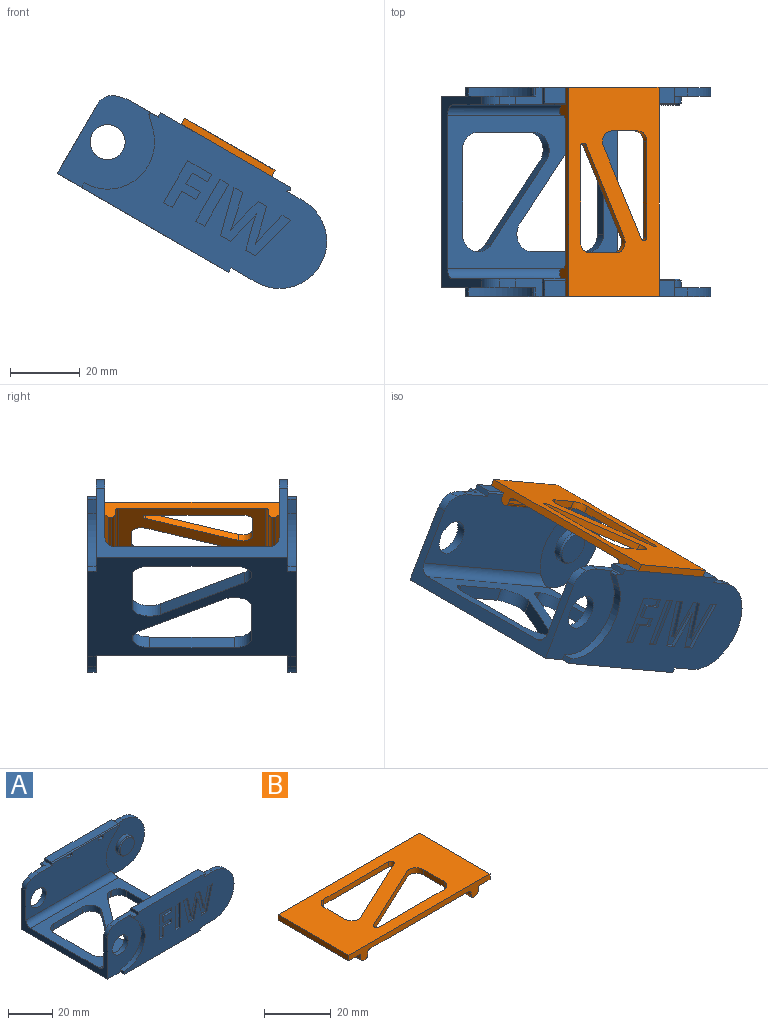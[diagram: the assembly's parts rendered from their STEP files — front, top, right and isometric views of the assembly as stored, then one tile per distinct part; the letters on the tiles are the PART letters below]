
ASSEMBLY  parts=2 mates=1
PART A: 175 faces, bbox 78.6x60x30 mm
  f0: plane 70.56x30mm, normal (0,1,0), area 1436.2mm2, adj f4,f7,f8,f9,f10,f11,f19,f20
  f1: plane 70.56x30mm, normal (0,-1,0), area 1436.2mm2, adj f4,f6,f13,f14,f15,f16,f25,f26
  f2: plane 60.26x23mm, normal (0,-1,0), area 1123.2mm2, adj f5,f20,f24,f28,f31,f42,f43,f63
  f3: plane 56.37x44mm, normal (0,0,1), area 1118.5mm2, adj f5,f46,f47,f48,f49,f50,f51,f52
  f4: plane 60x56.81mm, normal (0,0,-1), area 1989.1mm2, adj f0,f1,f5,f8,f13,f17,f19,f23
  f5: plane 55x22.95mm, normal (-1,0,0), area 293.6mm2, adj f2,f3,f4,f12,f17,f23,f62,f63
  f6: plane 42.97x4.5mm, normal (0,0,1), area 193.4mm2, adj f1,f16,f86,f88
  f7: plane 42.97x4.5mm, normal (0,0,1), area 193.4mm2, adj f0,f20,f87,f89
  f8: plane 2.5x1.5mm, normal (1,0,0), area 3.8mm2, adj f0,f4,f9,f35
  f9: plane 8.25x2.5mm, normal (0,0,-1), area 20.6mm2, adj f0,f8,f11,f35
  f10: plane 5.59x2.5mm, normal (0,0,1), area 14mm2, adj f0,f11,f28,f35
  f11: cylinder r=13.5mm len=27mm, axis (0,-1,0), area 106mm2, adj f0,f9,f10,f35
  f12: plane 60.26x23mm, normal (0,1,0), area 1123.2mm2, adj f5,f16,f18,f27,f33,f44,f45,f62
  f13: plane 2.5x1.5mm, normal (-1,0,0), area 3.7mm2, adj f1,f4,f14,f17
  f14: cylinder r=13.5mm len=23.05mm, axis (0,-1,0), area 79.5mm2, adj f1,f13,f15,f17
  f15: plane 3.1x3.1mm, normal (-0.71,0,-0.71), area 11mm2, adj f1,f14,f17,f64
  f16: plane 5x1.5mm, normal (-1,0,0), area 7.4mm2, adj f1,f6,f12,f44,f86
  f17: plane 28.5x21.5mm, normal (0,-1,0), area 430.1mm2, adj f4,f5,f13,f14,f15,f18,f44,f45
  f18: cylinder r=5.05mm len=10.1mm, axis (0,-1,0), area 79.3mm2, adj f12,f17
  f19: plane 2.5x1.5mm, normal (-1,0,0), area 3.7mm2, adj f0,f4,f22,f23
  f20: plane 5x1.5mm, normal (-1,0,0), area 7.4mm2, adj f0,f2,f7,f42,f87
  f21: plane 3.1x3.1mm, normal (-0.71,0,-0.71), area 11mm2, adj f0,f22,f23,f65
  f22: cylinder r=13.5mm len=23.05mm, axis (0,1,0), area 79.5mm2, adj f0,f19,f21,f23
  f23: plane 28.5x21.5mm, normal (0,1,0), area 430.1mm2, adj f4,f5,f19,f21,f22,f24,f42,f43
  f24: cylinder r=5.05mm len=10.1mm, axis (0,1,0), area 79.3mm2, adj f2,f23
  f25: plane 2.5x1.5mm, normal (1,0,0), area 3.8mm2, adj f1,f4,f26,f34
  f26: plane 8.25x2.5mm, normal (0,0,-1), area 20.6mm2, adj f1,f25,f30,f34
  f27: plane 5x4.75mm, normal (0.71,0,-0.71), area 19.6mm2, adj f1,f12,f29,f33,f34,f88
  f28: plane 5x4.75mm, normal (0.71,0,-0.71), area 19.6mm2, adj f0,f2,f10,f31,f35,f89
  f29: plane 5.59x2.5mm, normal (0,0,1), area 14mm2, adj f1,f27,f30,f34
  f30: cylinder r=13.5mm len=27mm, axis (0,-1,0), area 106mm2, adj f1,f26,f29,f34
  f31: cylinder r=13.5mm len=18.72mm, axis (0,1,0), area 51.8mm2, adj f2,f28,f35,f63,f174
  f32: plane 55x2.43mm, normal (1,0,0), area 133.4mm2, adj f4,f34,f35,f174
  f33: cylinder r=13.5mm len=18.72mm, axis (0,1,0), area 51.8mm2, adj f12,f27,f34,f62,f174
  f34: plane 28.5x27mm, normal (0,1,0), area 507.3mm2, adj f4,f25,f26,f27,f29,f30,f32,f33
  f35: plane 28.5x27mm, normal (0,-1,0), area 507.3mm2, adj f4,f8,f9,f10,f11,f28,f31,f32
  f36: cylinder r=5mm len=10mm, axis (0,1,0), area 62.8mm2, adj f35,f38
  f37: plane 9x9mm, normal (0,-1,0), area 63.6mm2, adj f38
  f38: cone r=4.5mm half-angle=45deg, axis (0,1,0), area 21.1mm2, adj f36,f37
  f39: cylinder r=5mm len=10mm, axis (0,-1,0), area 62.8mm2, adj f34,f41
  f40: plane 9x9mm, normal (0,1,0), area 63.6mm2, adj f41
  f41: cone r=5mm half-angle=45deg, axis (0,-1,0), area 21.1mm2, adj f39,f40
  f42: plane 9x5mm, normal (0,0,1), area 28mm2, adj f0,f2,f20,f23,f43,f65
  f43: cylinder r=13.5mm len=4.76mm, axis (0,-1,0), area 12.2mm2, adj f2,f23,f42,f173
  f44: plane 9x5mm, normal (0,0,1), area 28mm2, adj f1,f12,f16,f17,f45,f64
  f45: cylinder r=13.5mm len=4.76mm, axis (0,-1,0), area 12.2mm2, adj f12,f17,f44,f172
  f46: plane 18.74x3.5mm, normal (0,-1,0), area 65.6mm2, adj f3,f4,f58,f61
  f47: plane 24.25x3.5mm, normal (1,0,0), area 84.9mm2, adj f3,f4,f60,f61
  f48: plane 3.5x0.5mm, normal (0,1,0), area 1.8mm2, adj f3,f4,f59,f60
  f49: plane 24.25x18.24mm, normal (-0.8,0.6,0), area 106.2mm2, adj f3,f4,f58,f59
  f50: plane 24.25x18.24mm, normal (0.8,-0.6,0), area 106.2mm2, adj f3,f4,f54,f57
  f51: plane 18.74x3.5mm, normal (0,1,0), area 65.6mm2, adj f3,f4,f54,f55
  f52: plane 24.25x3.5mm, normal (-1,0,0), area 84.9mm2, adj f3,f4,f55,f56
  f53: plane 3.5x0.5mm, normal (0,-1,0), area 1.8mm2, adj f3,f4,f56,f57
  f54: cylinder r=5mm len=8.01mm, axis (0,0,1), area 38.8mm2, adj f3,f4,f50,f51
  f55: cylinder r=5mm len=5mm, axis (0,0,-1), area 27.5mm2, adj f3,f4,f51,f52
  f56: cylinder r=5mm len=5mm, axis (0,0,1), area 27.5mm2, adj f3,f4,f52,f53
  f57: cylinder r=5mm len=4mm, axis (0,0,-1), area 16.2mm2, adj f3,f4,f50,f53
  f58: cylinder r=5mm len=8.01mm, axis (0,0,1), area 38.8mm2, adj f3,f4,f46,f49
  f59: cylinder r=5mm len=4mm, axis (0,0,-1), area 16.2mm2, adj f3,f4,f48,f49
  f60: cylinder r=5mm len=5mm, axis (0,0,-1), area 27.5mm2, adj f3,f4,f47,f48
  f61: cylinder r=5mm len=5mm, axis (0,0,1), area 27.5mm2, adj f3,f4,f46,f47
  f62: cylinder r=3mm len=56.37mm, axis (-1,0,0), area 263.3mm2, adj f3,f5,f12,f33,f174
  f63: cylinder r=3mm len=56.37mm, axis (1,0,0), area 263.3mm2, adj f2,f3,f5,f31,f174
  f64: cylinder r=0.5mm len=2.5mm, axis (0,1,0), area 2.9mm2, adj f1,f15,f17,f44
  f65: cylinder r=0.5mm len=2.5mm, axis (0,1,0), area 2.9mm2, adj f0,f21,f23,f42
  f66: plane 3x3mm, normal (0,0,-1), area 9mm2, adj f2,f67,f69,f70
  f67: plane 3x1.5mm, normal (1,0,0), area 4.5mm2, adj f2,f66,f68,f70
  f68: plane 3x3mm, normal (0,0,1), area 9mm2, adj f2,f67,f69,f70
  f69: plane 3x1.5mm, normal (-1,0,0), area 4.5mm2, adj f2,f66,f68,f70
  f70: plane 3x1.5mm, normal (0,-1,0), area 4.5mm2, adj f66,f67,f68,f69
  f71: plane 3x3mm, normal (0,0,-1), area 9mm2, adj f2,f72,f74,f75
  f72: plane 3x1.5mm, normal (1,0,0), area 4.5mm2, adj f2,f71,f73,f75
  f73: plane 3x3mm, normal (0,0,1), area 9mm2, adj f2,f72,f74,f75
  f74: plane 3x1.5mm, normal (-1,0,0), area 4.5mm2, adj f2,f71,f73,f75
  f75: plane 3x1.5mm, normal (0,-1,0), area 4.5mm2, adj f71,f72,f73,f74
  f76: plane 3x3mm, normal (0,0,-1), area 9mm2, adj f12,f77,f79,f80
  f77: plane 3x1.5mm, normal (-1,0,0), area 4.5mm2, adj f12,f76,f78,f80
  f78: plane 3x3mm, normal (0,0,1), area 9mm2, adj f12,f77,f79,f80
  f79: plane 3x1.5mm, normal (1,0,0), area 4.5mm2, adj f12,f76,f78,f80
  f80: plane 3x1.5mm, normal (0,1,0), area 4.5mm2, adj f76,f77,f78,f79
  f81: plane 3x3mm, normal (0,0,-1), area 9mm2, adj f12,f82,f84,f85
  f82: plane 3x1.5mm, normal (-1,0,0), area 4.5mm2, adj f12,f81,f83,f85
  f83: plane 3x3mm, normal (0,0,1), area 9mm2, adj f12,f82,f84,f85
  f84: plane 3x1.5mm, normal (1,0,0), area 4.5mm2, adj f12,f81,f83,f85
  f85: plane 3x1.5mm, normal (0,1,0), area 4.5mm2, adj f81,f82,f83,f84
  f86: plane 43.18x0.5mm, normal (0,0.71,0.71), area 30.5mm2, adj f6,f12,f16,f88
  f87: plane 43.18x0.5mm, normal (0,-0.71,0.71), area 30.5mm2, adj f2,f7,f20,f89
  f88: plane 5x0.71mm, normal (0.92,0,0.38), area 3.7mm2, adj f1,f6,f12,f27,f86
  f89: plane 5x0.71mm, normal (0.92,0,0.38), area 3.7mm2, adj f0,f2,f7,f28,f87
  f90: plane 3.35x1mm, normal (0,0,1), area 3.4mm2, adj f1,f91,f113,f114
  f91: plane 13.88x3.53mm, normal (-0.97,0,0.25), area 14.3mm2, adj f1,f90,f92,f114
  f92: plane 2.9x1mm, normal (0,0,-1), area 2.9mm2, adj f1,f91,f93,f114
  f93: plane 7.58x1.77mm, normal (0.97,0,-0.23), area 7.8mm2, adj f1,f92,f94,f114
  f94: extruded ~1.79x1mm, area 1.8mm2, adj f1,f93,f95,f114
  f95: extruded ~1.85x1mm, area 1.9mm2, adj f1,f94,f96,f114
  f96: extruded ~1.84x1mm, area 1.9mm2, adj f1,f95,f97,f114
  f97: extruded ~1.59x1mm, area 1.6mm2, adj f1,f96,f98,f114
  f98: plane 7.78x2.02mm, normal (-0.97,0,-0.25), area 8mm2, adj f1,f97,f99,f114
  f99: plane 2.78x1mm, normal (0,0,-1), area 2.8mm2, adj f1,f98,f100,f114
  f100: plane 7.78x2.02mm, normal (0.97,0,-0.25), area 8mm2, adj f1,f99,f101,f114
  f101: extruded ~1.76x1mm, area 1.8mm2, adj f1,f100,f102,f114
  f102: extruded ~1.68x1mm, area 1.7mm2, adj f1,f101,f103,f114
  f103: extruded ~3.64x1mm, area 3.7mm2, adj f1,f102,f104,f114
  f104: plane 7.58x1.78mm, normal (-0.97,0,-0.23), area 7.8mm2, adj f1,f103,f105,f114
  f105: plane 2.9x1mm, normal (0,0,-1), area 2.9mm2, adj f1,f104,f106,f114
  f106: plane 13.88x3.54mm, normal (0.97,0,0.25), area 14.3mm2, adj f1,f105,f107,f114
  f107: plane 3.34x1mm, normal (0,0,1), area 3.3mm2, adj f1,f106,f108,f114
  f108: plane 7.27x1.87mm, normal (-0.97,0,0.25), area 7.5mm2, adj f1,f107,f109,f114
  f109: extruded ~1.62x1mm, area 1.7mm2, adj f1,f108,f110,f114
  f110: extruded ~1.65x1mm, area 1.7mm2, adj f1,f109,f111,f114
  f111: extruded ~1.64x1mm, area 1.7mm2, adj f1,f110,f112,f114
  f112: extruded ~1.61x1mm, area 1.6mm2, adj f1,f111,f113,f114
  f113: plane 7.29x1.88mm, normal (0.97,0,0.25), area 7.5mm2, adj f1,f90,f112,f114
  f114: plane 18.8x13.88mm, normal (0,-1,0), area 133.3mm2, adj f90,f91,f92,f93,f94,f95,f96,f97
  f115: plane 13.88x1mm, normal (1,0,0), area 13.9mm2, adj f1,f116,f118,f119
  f116: plane 2.94x1mm, normal (0,0,1), area 2.9mm2, adj f1,f115,f117,f119
  f117: plane 13.88x1mm, normal (-1,0,0), area 13.9mm2, adj f1,f116,f118,f119
  f118: plane 2.94x1mm, normal (0,0,-1), area 2.9mm2, adj f1,f115,f117,f119
  f119: plane 13.88x2.94mm, normal (0,-1,0), area 40.9mm2, adj f115,f116,f117,f118
  f120: plane 2.9x1mm, normal (0,0,1), area 2.9mm2, adj f1,f121,f129,f130
  f121: plane 5.49x1mm, normal (-1,0,0), area 5.5mm2, adj f1,f120,f122,f130
  f122: plane 4.71x1mm, normal (0,0,1), area 4.7mm2, adj f1,f121,f123,f130
  f123: plane 2.4x1mm, normal (-1,0,0), area 2.4mm2, adj f1,f122,f124,f130
  f124: plane 4.71x1mm, normal (0,0,-1), area 4.7mm2, adj f1,f123,f125,f130
  f125: plane 3.58x1mm, normal (-1,0,0), area 3.6mm2, adj f1,f124,f126,f130
  f126: plane 5.06x1mm, normal (0,0,1), area 5.1mm2, adj f1,f125,f127,f130
  f127: plane 2.41x1mm, normal (-1,0,0), area 2.4mm2, adj f1,f126,f128,f130
  f128: plane 7.96x1mm, normal (0,0,-1), area 8mm2, adj f1,f127,f129,f130
  f129: plane 13.88x1mm, normal (1,0,0), area 13.9mm2, adj f1,f120,f128,f130
  f130: plane 13.88x7.96mm, normal (0,-1,0), area 63.7mm2, adj f120,f121,f122,f123,f124,f125,f126,f127
  f131: plane 3.35x1mm, normal (0,0,1), area 3.4mm2, adj f0,f132,f154,f155
  f132: plane 13.88x3.53mm, normal (0.97,0,0.25), area 14.3mm2, adj f0,f131,f133,f155
  f133: plane 2.9x1mm, normal (0,0,-1), area 2.9mm2, adj f0,f132,f134,f155
  f134: plane 7.58x1.77mm, normal (-0.97,0,-0.23), area 7.8mm2, adj f0,f133,f135,f155
  f135: extruded ~1.79x1mm, area 1.8mm2, adj f0,f134,f136,f155
  f136: extruded ~1.85x1mm, area 1.9mm2, adj f0,f135,f137,f155
  f137: extruded ~1.84x1mm, area 1.9mm2, adj f0,f136,f138,f155
  f138: extruded ~1.59x1mm, area 1.6mm2, adj f0,f137,f139,f155
  f139: plane 7.78x2.02mm, normal (0.97,0,-0.25), area 8mm2, adj f0,f138,f140,f155
  f140: plane 2.78x1mm, normal (0,0,-1), area 2.8mm2, adj f0,f139,f141,f155
  f141: plane 7.78x2.02mm, normal (-0.97,0,-0.25), area 8mm2, adj f0,f140,f142,f155
  f142: extruded ~1.76x1mm, area 1.8mm2, adj f0,f141,f143,f155
  f143: extruded ~1.68x1mm, area 1.7mm2, adj f0,f142,f144,f155
  f144: extruded ~3.64x1mm, area 3.7mm2, adj f0,f143,f145,f155
  f145: plane 7.58x1.78mm, normal (0.97,0,-0.23), area 7.8mm2, adj f0,f144,f146,f155
  f146: plane 2.9x1mm, normal (0,0,-1), area 2.9mm2, adj f0,f145,f147,f155
  f147: plane 13.88x3.54mm, normal (-0.97,0,0.25), area 14.3mm2, adj f0,f146,f148,f155
  f148: plane 3.34x1mm, normal (0,0,1), area 3.3mm2, adj f0,f147,f149,f155
  f149: plane 7.27x1.87mm, normal (0.97,0,0.25), area 7.5mm2, adj f0,f148,f150,f155
  f150: extruded ~1.62x1mm, area 1.7mm2, adj f0,f149,f151,f155
  f151: extruded ~1.65x1mm, area 1.7mm2, adj f0,f150,f152,f155
  f152: extruded ~1.64x1mm, area 1.7mm2, adj f0,f151,f153,f155
  f153: extruded ~1.61x1mm, area 1.6mm2, adj f0,f152,f154,f155
  f154: plane 7.29x1.88mm, normal (-0.97,0,0.25), area 7.5mm2, adj f0,f131,f153,f155
  f155: plane 18.8x13.88mm, normal (0,1,0), area 133.3mm2, adj f131,f132,f133,f134,f135,f136,f137,f138
  f156: plane 13.88x1mm, normal (-1,0,0), area 13.9mm2, adj f0,f157,f159,f160
  f157: plane 2.94x1mm, normal (0,0,1), area 2.9mm2, adj f0,f156,f158,f160
  f158: plane 13.88x1mm, normal (1,0,0), area 13.9mm2, adj f0,f157,f159,f160
  f159: plane 2.94x1mm, normal (0,0,-1), area 2.9mm2, adj f0,f156,f158,f160
  f160: plane 13.88x2.94mm, normal (0,1,0), area 40.9mm2, adj f156,f157,f158,f159
  f161: plane 2.9x1mm, normal (0,0,1), area 2.9mm2, adj f0,f162,f170,f171
  f162: plane 5.49x1mm, normal (1,0,0), area 5.5mm2, adj f0,f161,f163,f171
  f163: plane 4.71x1mm, normal (0,0,1), area 4.7mm2, adj f0,f162,f164,f171
  f164: plane 2.4x1mm, normal (1,0,0), area 2.4mm2, adj f0,f163,f165,f171
  f165: plane 4.71x1mm, normal (0,0,-1), area 4.7mm2, adj f0,f164,f166,f171
  f166: plane 3.58x1mm, normal (1,0,0), area 3.6mm2, adj f0,f165,f167,f171
  f167: plane 5.06x1mm, normal (0,0,1), area 5.1mm2, adj f0,f166,f168,f171
  f168: plane 2.41x1mm, normal (1,0,0), area 2.4mm2, adj f0,f167,f169,f171
  f169: plane 7.96x1mm, normal (0,0,-1), area 8mm2, adj f0,f168,f170,f171
  f170: plane 13.88x1mm, normal (-1,0,0), area 13.9mm2, adj f0,f161,f169,f171
  f171: plane 13.88x7.96mm, normal (0,1,0), area 63.7mm2, adj f161,f162,f163,f164,f165,f166,f167,f168
  f172: cylinder r=5mm len=4.68mm, axis (0,-1,0), area 15.1mm2, adj f5,f12,f17,f45
  f173: cylinder r=5mm len=4.68mm, axis (0,-1,0), area 15.1mm2, adj f2,f5,f23,f43
  f174: cylinder r=5mm len=55mm, axis (0,1,0), area 76.9mm2, adj f3,f31,f32,f33,f34,f35,f62,f63
PART B: 56 faces, bbox 60x30x5 mm
  f0: plane 60x30mm, normal (0,0,1), area 1243.8mm2, adj f3,f4,f7,f8,f40,f41,f42,f43
  f1: plane 42x30mm, normal (0,0,-1), area 703.8mm2, adj f3,f4,f40,f41,f42,f43,f44,f45
  f2: plane 30x2mm, normal (1,0,0), area 56mm2, adj f3,f4,f25,f26,f27,f29,f32,f33
  f3: plane 60x5mm, normal (0,1,0), area 137mm2, adj f0,f1,f2,f5,f6,f7,f8,f9
  f4: plane 60x5mm, normal (0,-1,0), area 137mm2, adj f0,f1,f2,f5,f6,f7,f8,f9
  f5: plane 30x1mm, normal (0,0,-1), area 30mm2, adj f3,f4,f39,f53
  f6: plane 30x1mm, normal (0,0,-1), area 30mm2, adj f3,f4,f38,f52
  f7: plane 30x2mm, normal (-1,0,0), area 60mm2, adj f0,f3,f4,f12
  f8: plane 30x2mm, normal (1,0,0), area 60mm2, adj f0,f3,f4,f25
  f9: plane 30x1mm, normal (1,0,0), area 30mm2, adj f3,f4,f53,f55
  f10: plane 30x1mm, normal (-1,0,0), area 30mm2, adj f3,f4,f52,f54
  f11: plane 30x2mm, normal (-1,0,0), area 56mm2, adj f3,f4,f12,f13,f14,f16,f19,f20
  f12: plane 30x5mm, normal (0,0,-1), area 150mm2, adj f3,f4,f7,f11
  f13: plane 2x1.5mm, normal (0,0,1), area 3mm2, adj f11,f14,f16,f17
  f14: plane 1.5x1mm, normal (0,1,0), area 1.4mm2, adj f11,f13,f15,f17,f24
  f15: plane 2x1mm, normal (0,0,-1), area 2mm2, adj f14,f16,f24,f39
  f16: plane 1.5x1mm, normal (0,-1,0), area 1.4mm2, adj f11,f13,f15,f17,f24
  f17: plane 2x0.5mm, normal (-1,0,0), area 1mm2, adj f13,f14,f16,f24
  f18: plane 2x1mm, normal (0,0,-1), area 2mm2, adj f19,f21,f23,f39
  f19: plane 1.5x1mm, normal (0,-1,0), area 1.4mm2, adj f11,f18,f20,f22,f23
  f20: plane 2x1.5mm, normal (0,0,1), area 3mm2, adj f11,f19,f21,f22
  f21: plane 1.5x1mm, normal (0,1,0), area 1.4mm2, adj f11,f18,f20,f22,f23
  f22: plane 2x0.5mm, normal (-1,0,0), area 1mm2, adj f19,f20,f21,f23
  f23: plane 2x0.5mm, normal (-0.71,0,-0.71), area 1.4mm2, adj f18,f19,f21,f22
  f24: plane 2x0.5mm, normal (-0.71,0,-0.71), area 1.4mm2, adj f14,f15,f16,f17
  f25: plane 30x5mm, normal (0,0,-1), area 150mm2, adj f2,f3,f4,f8
  f26: plane 2x1.5mm, normal (0,0,1), area 3mm2, adj f2,f27,f29,f30
  f27: plane 1.5x1mm, normal (0,-1,0), area 1.4mm2, adj f2,f26,f28,f30,f37
  f28: plane 2x1mm, normal (0,0,-1), area 2mm2, adj f27,f29,f37,f38
  f29: plane 1.5x1mm, normal (0,1,0), area 1.4mm2, adj f2,f26,f28,f30,f37
  f30: plane 2x0.5mm, normal (1,0,0), area 1mm2, adj f26,f27,f29,f37
  f31: plane 2x1mm, normal (0,0,-1), area 2mm2, adj f32,f34,f36,f38
  f32: plane 1.5x1mm, normal (0,1,0), area 1.4mm2, adj f2,f31,f33,f35,f36
  f33: plane 2x1.5mm, normal (0,0,1), area 3mm2, adj f2,f32,f34,f35
  f34: plane 1.5x1mm, normal (0,-1,0), area 1.4mm2, adj f2,f31,f33,f35,f36
  f35: plane 2x0.5mm, normal (1,0,0), area 1mm2, adj f32,f33,f34,f36
  f36: plane 2x0.5mm, normal (0.71,0,-0.71), area 1.4mm2, adj f31,f32,f34,f35
  f37: plane 2x0.5mm, normal (0.71,0,-0.71), area 1.4mm2, adj f27,f28,f29,f30
  f38: plane 30x1mm, normal (0.71,0,-0.71), area 42.4mm2, adj f2,f3,f4,f6,f28,f31
  f39: plane 30x1mm, normal (-0.71,0,-0.71), area 42.4mm2, adj f3,f4,f5,f11,f15,f18
  f40: plane 27.53x2mm, normal (0,-1,0), area 55.1mm2, adj f0,f1,f49,f51
  f41: plane 8.75x2mm, normal (1,0,0), area 17.5mm2, adj f0,f1,f48,f49
  f42: plane 26.68x12.56mm, normal (-0.43,0.9,0), area 59mm2, adj f0,f1,f48,f51
  f43: plane 27.53x2mm, normal (0,1,0), area 55.1mm2, adj f0,f1,f46,f50
  f44: plane 8.75x2mm, normal (-1,0,0), area 17.5mm2, adj f0,f1,f46,f47
  f45: plane 26.68x12.56mm, normal (0.43,-0.9,0), area 59mm2, adj f0,f1,f47,f50
  f46: cylinder r=3mm len=3mm, axis (0,0,1), area 9.4mm2, adj f0,f1,f43,f44
  f47: cylinder r=3mm len=4.28mm, axis (0,0,1), area 12.1mm2, adj f0,f1,f44,f45
  f48: cylinder r=3mm len=4.28mm, axis (0,0,1), area 12.1mm2, adj f0,f1,f41,f42
  f49: cylinder r=3mm len=3mm, axis (0,0,1), area 9.4mm2, adj f0,f1,f40,f41
  f50: cylinder r=1mm len=2mm, axis (0,0,-1), area 5.4mm2, adj f0,f1,f43,f45
  f51: cylinder r=1mm len=2mm, axis (0,0,-1), area 5.4mm2, adj f0,f1,f40,f42
  f52: cylinder r=1mm len=30mm, axis (0,-1,0), area 47.1mm2, adj f3,f4,f6,f10
  f53: cylinder r=1mm len=30mm, axis (0,1,0), area 47.1mm2, adj f3,f4,f5,f9
  f54: cylinder r=1mm len=30mm, axis (0,-1,0), area 47.1mm2, adj f1,f3,f4,f10
  f55: cylinder r=1mm len=30mm, axis (0,1,0), area 47.1mm2, adj f1,f3,f4,f9
PLACE A rot(axis=(0,1,0),30deg) t=(31.02,39.88,-17.15)mm fixed
PLACE B rot(axis=(-0.25,0.25,-0.94),93.8deg) t=(66.61,39.88,-6.5)mm
MATE planar A.f77 <-> B.f29  axis (-0.87,0,0.5) through (76.75,14.88,-10.93)mm
